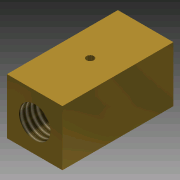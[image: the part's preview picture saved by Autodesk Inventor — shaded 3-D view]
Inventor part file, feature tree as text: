
AUTODESK INVENTOR PART (.ipt)
format: ipt  version: 2011 (Build 150239000, 239)  size: 83,968 bytes
history: native  units: in
note: dims shown in document units (in); Inventor stores cm internally (conversion verified against a paired STEP export)
features: extrude x2, sketch x2, thread x1
ambient origin geometry x8: Origin, YZ Plane, XZ Plane, XY Plane, X Axis, Y Axis, Z Axis, Center Point
bodies: Solid1 (feature_tree)
feature tree (5):
  extrude  "Extrusion1"  Depth=0.75in
  extrude  "Extrusion2"  Depth=1.5in TaperAngle=0.0deg
  thread  "Thread1"  [1 undecoded]
  sketch  "Sketch1"  dims[d0=0.75in d1=0.75in]
  sketch  "Sketch2"  dims[d2=0.425in d3=1.5in d4=0.0in d5=0.1in d6=0.25in d7=0.0in d8=1.0in d9=0.0in]
note: 1 required parameter value undecoded (feature->parameter linkage not recoverable at this tier; creation-order binding heuristic only, values carry confidence <= 0.55)
